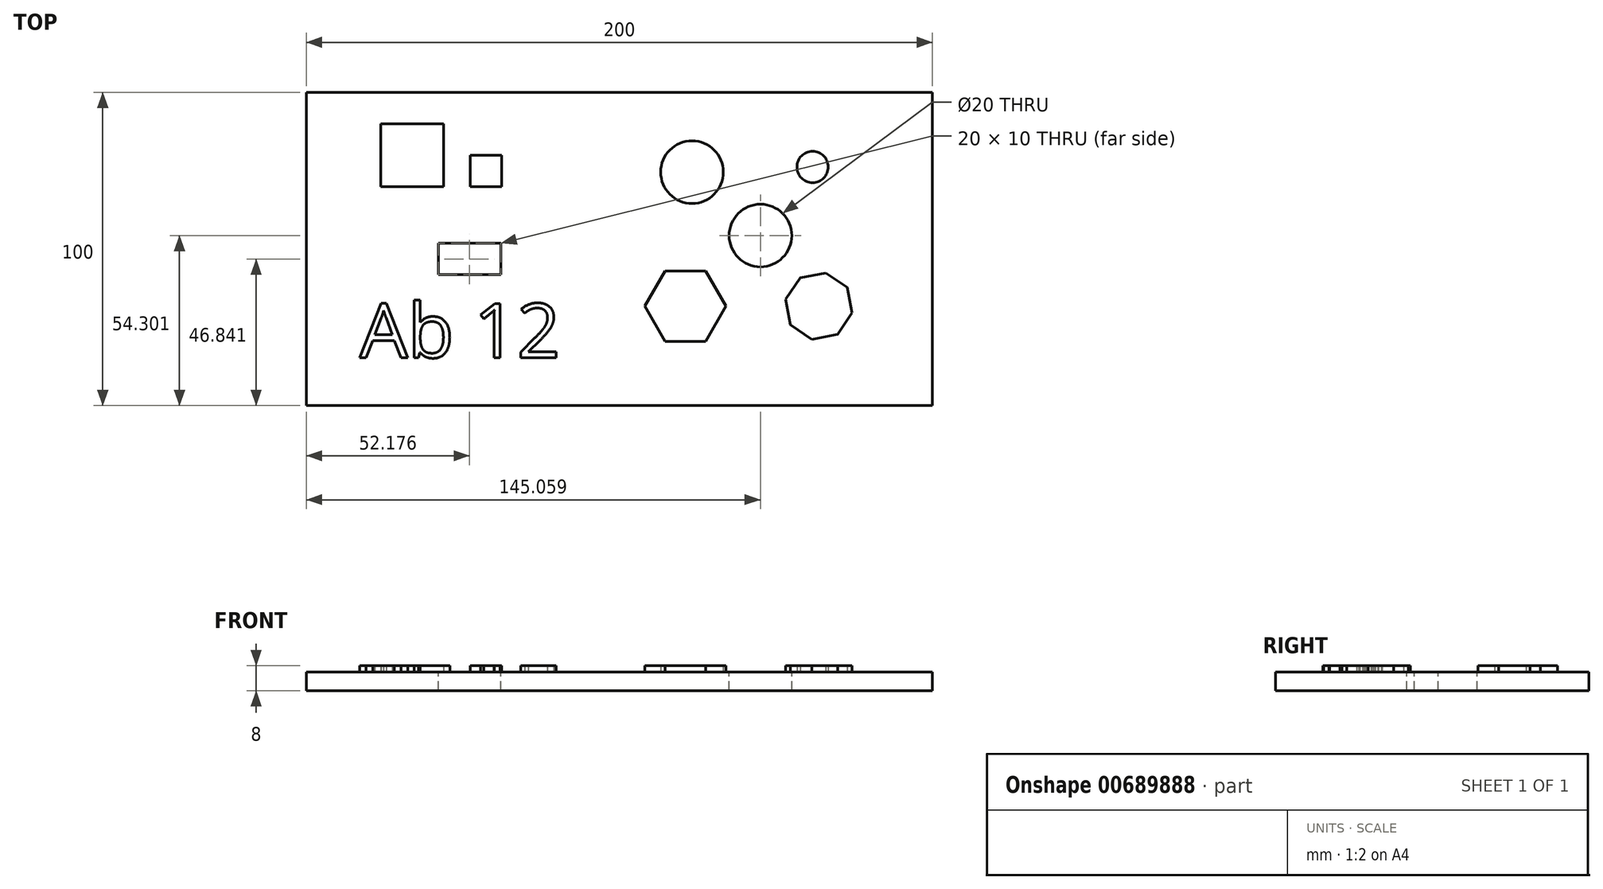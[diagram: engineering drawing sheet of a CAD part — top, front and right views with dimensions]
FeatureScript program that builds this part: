
annotation { "Feature Type Name" : "Feature", "Feature Type Description" : "" }
export const myFeature = defineFeature(function(context is Context, id is Id, definition is map)
    precondition{}
    {
        {
            var Q0;
            Q0=qCreatedBy(makeId("Top.planeOp"),FACE);
            var sketch = newSketch(context, id + "F0", { "sketchPlane" : qUnion([Q0])});
            skLineSegment(sketch, "E0.bottom", {"start": v(-100, 50) * mm, "end": v(100, 50) * mm});
            skLineSegment(sketch, "E0.top", {"start": v(-100, -50) * mm, "end": v(100, -50) * mm});
            skLineSegment(sketch, "E0.left", {"start": v(-100, 50) * mm, "end": v(-100, -50) * mm});
            skLineSegment(sketch, "E0.right", {"start": v(100, 50) * mm, "end": v(100, -50) * mm});
            skSolve(sketch);
        }
        {
            var Q0;
            Q0=makeQuery(id+"F0.imprint","IMPRINT",FACE,{"disambiguationData":[TD([[makeQuery(id+"F0.imprint","IMPRINT",EDGE,{"derivedFrom":sQuery(id+"F0.wireOp",EDGE,"E0.bottom")}),-1.0]])]});
            extrude(context, id + "F1", {"entities" : qUnion([Q0]), "depth" : 6 * mm, "offsetDistance" : 25 * mm});
        }
        {
            var Q0;
            Q0=makeQuery(id+"F1.opExtrude","CAP_FACE",FACE,{"disambiguationData":[OSD([sQuery(id+"F0.wireOp",EDGE,"E0.bottom"),sQuery(id+"F0.wireOp",EDGE,"E0.top"),sQuery(id+"F0.wireOp",EDGE,"E0.left"),sQuery(id+"F0.wireOp",EDGE,"E0.right")])],"isStart":false});
            var sketch = newSketch(context, id + "F2", { "sketchPlane" : qUnion([Q0])});
            skLineSegment(sketch, "E1.bottom", {"start": v(-76.17, 39.96) * mm, "end": v(-56.17, 39.96) * mm});
            skLineSegment(sketch, "E1.top", {"start": v(-76.17, 19.96) * mm, "end": v(-56.17, 19.96) * mm});
            skLineSegment(sketch, "E1.left", {"start": v(-76.17, 39.96) * mm, "end": v(-76.17, 19.96) * mm});
            skLineSegment(sketch, "E1.right", {"start": v(-56.17, 39.96) * mm, "end": v(-56.17, 19.96) * mm});
            skLineSegment(sketch, "E2.bottom", {"start": v(-47.63, 29.96) * mm, "end": v(-37.63, 29.96) * mm});
            skLineSegment(sketch, "E2.top", {"start": v(-47.63, 19.96) * mm, "end": v(-37.63, 19.96) * mm});
            skLineSegment(sketch, "E2.left", {"start": v(-47.63, 29.96) * mm, "end": v(-47.63, 19.96) * mm});
            skLineSegment(sketch, "E2.right", {"start": v(-37.63, 29.96) * mm, "end": v(-37.63, 19.96) * mm});
            skCircle(sketch, "E3", {"center": v(23.2, 24.54) * mm, "radius": 10 * mm});
            skCircle(sketch, "E4", {"center": v(61.7, 26.18) * mm, "radius": 5 * mm});
            skCircle(sketch, "E5.cCircle", {"center": v(21.07, -18.23) * mm, "radius": 11.24 * mm, "construction": true});
            skLineSegment(sketch, "E5.0", {"start": v(34.05, -18.21) * mm, "end": v(27.58, -29.46) * mm});
            skLineSegment(sketch, "E5.1", {"start": v(27.58, -29.46) * mm, "end": v(14.6, -29.48) * mm});
            skLineSegment(sketch, "E5.2", {"start": v(14.6, -29.48) * mm, "end": v(8.1, -18.26) * mm});
            skLineSegment(sketch, "E5.3", {"start": v(8.1, -18.26) * mm, "end": v(14.57, -7) * mm});
            skLineSegment(sketch, "E5.4", {"start": v(14.57, -7) * mm, "end": v(27.54, -6.98) * mm});
            skLineSegment(sketch, "E5.5", {"start": v(27.54, -6.98) * mm, "end": v(34.05, -18.21) * mm});
            skPoint(sketch, "E5.0.midPoint", {"position": v(30.82, -23.84) * mm});
            skCircle(sketch, "E6.cCircle", {"center": v(63.7, -18.23) * mm, "radius": 10 * mm, "construction": true});
            skLineSegment(sketch, "E6.0", {"start": v(74.3, -20.4) * mm, "end": v(69.66, -27.27) * mm});
            skLineSegment(sketch, "E6.1", {"start": v(69.66, -27.27) * mm, "end": v(61.53, -28.84) * mm});
            skLineSegment(sketch, "E6.2", {"start": v(61.53, -28.84) * mm, "end": v(54.66, -24.2) * mm});
            skLineSegment(sketch, "E6.3", {"start": v(54.66, -24.2) * mm, "end": v(53.1, -16.06) * mm});
            skLineSegment(sketch, "E6.4", {"start": v(53.1, -16.06) * mm, "end": v(57.74, -9.2) * mm});
            skLineSegment(sketch, "E6.5", {"start": v(57.74, -9.2) * mm, "end": v(65.87, -7.63) * mm});
            skLineSegment(sketch, "E6.6", {"start": v(65.87, -7.63) * mm, "end": v(72.73, -12.27) * mm});
            skLineSegment(sketch, "E6.7", {"start": v(72.73, -12.27) * mm, "end": v(74.3, -20.4) * mm});
            skPoint(sketch, "E6.0.midPoint", {"position": v(71.98, -23.84) * mm});
            skSolve(sketch);
        }
        {
            var Q0;
            Q0=makeQuery(id+"F2.imprint","IMPRINT",FACE,{"disambiguationData":[TD([[makeQuery(id+"F2.imprint","IMPRINT",EDGE,{"derivedFrom":sQuery(id+"F2.wireOp",EDGE,"E1.bottom")}),-1.0]])]});
            extrude(context, id + "F3", {"entities" : qUnion([Q0]), "operationType" : NewBodyOperationType.ADD, "depth" : 2 * mm, "offsetDistance" : 25 * mm});
        }
        {
            var Q0;
            Q0=makeQuery(id+"F2.imprint","IMPRINT",FACE,{"disambiguationData":[TD([[makeQuery(id+"F2.imprint","IMPRINT",EDGE,{"derivedFrom":sQuery(id+"F2.wireOp",EDGE,"E2.bottom")}),-1.0]])]});
            extrude(context, id + "F4", {"entities" : qUnion([Q0]), "operationType" : NewBodyOperationType.ADD, "depth" : 2 * mm, "offsetDistance" : 25 * mm});
        }
        {
            var Q0;
            Q0=makeQuery(id+"F2.imprint","IMPRINT",FACE,{"disambiguationData":[TD([[makeQuery(id+"F2.imprint","IMPRINT",EDGE,{"derivedFrom":sQuery(id+"F2.wireOp",EDGE,"E3")}),1.0]])]});
            extrude(context, id + "F5", {"entities" : qUnion([Q0]), "operationType" : NewBodyOperationType.ADD, "depth" : 2 * mm, "offsetDistance" : 25 * mm});
        }
        {
            var Q0;
            Q0=makeQuery(id+"F2.imprint","IMPRINT",FACE,{"disambiguationData":[TD([[makeQuery(id+"F2.imprint","IMPRINT",EDGE,{"derivedFrom":sQuery(id+"F2.wireOp",EDGE,"E4")}),1.0]])]});
            extrude(context, id + "F6", {"entities" : qUnion([Q0]), "operationType" : NewBodyOperationType.ADD, "depth" : 2 * mm, "offsetDistance" : 25 * mm});
        }
        {
            var Q0;
            Q0=makeQuery(id+"F2.imprint","IMPRINT",FACE,{"disambiguationData":[TD([[makeQuery(id+"F2.imprint","IMPRINT",EDGE,{"derivedFrom":sQuery(id+"F2.wireOp",EDGE,"E5.0")}),-1.0]])]});
            extrude(context, id + "F7", {"entities" : qUnion([Q0]), "operationType" : NewBodyOperationType.ADD, "depth" : 2 * mm, "offsetDistance" : 25 * mm});
        }
        {
            var Q0;
            Q0=makeQuery(id+"F2.imprint","IMPRINT",FACE,{"disambiguationData":[TD([[makeQuery(id+"F2.imprint","IMPRINT",EDGE,{"derivedFrom":sQuery(id+"F2.wireOp",EDGE,"E6.0")}),-1.0]])]});
            extrude(context, id + "F8", {"entities" : qUnion([Q0]), "operationType" : NewBodyOperationType.ADD, "depth" : 2 * mm, "offsetDistance" : 25 * mm});
        }
        {
            var Q0;
            Q0=makeQuery(id+"F2.imprint","IMPRINT",FACE,{"disambiguationData":[TD([[makeQuery(id+"F2.imprint","IMPRINT",EDGE,{"derivedFrom":sQuery(id+"F2.wireOp",EDGE,"E1.bottom")}),1.0]])]});
            var sketch = newSketch(context, id + "F9", { "sketchPlane" : qUnion([Q0])});
            skText(sketch, "E7", { "text": "Ab 12", "fontName": "OpenSans-Regular.ttf"});
            const initialGuessF9  = {"E7": [-0.08292, -0.03468, 1, 0, 0.0174]};
            skSetInitialGuess(sketch, initialGuessF9);
            skSolve(sketch);
        }
        {
            var Q0;
            Q0 = qSketchRegion(id + "F9", true);
            extrude(context, id + "F10", {"entities" : qUnion([Q0]), "operationType" : NewBodyOperationType.ADD, "depth" : 2 * mm, "offsetDistance" : 25 * mm});
        }
        {
            var Q0;
            Q0=makeQuery(id+"F2.imprint","IMPRINT",FACE,{"disambiguationData":[TD([[makeQuery(id+"F2.imprint","IMPRINT",EDGE,{"derivedFrom":sQuery(id+"F2.wireOp",EDGE,"E1.bottom")}),1.0]])]});
            var sketch = newSketch(context, id + "F11", { "sketchPlane" : qUnion([Q0])});
            skLineSegment(sketch, "E8.bottom", {"start": v(-57.82, 1.84) * mm, "end": v(-37.82, 1.84) * mm});
            skLineSegment(sketch, "E8.top", {"start": v(-57.82, -8.16) * mm, "end": v(-37.82, -8.16) * mm});
            skLineSegment(sketch, "E8.left", {"start": v(-57.82, 1.84) * mm, "end": v(-57.82, -8.16) * mm});
            skLineSegment(sketch, "E8.right", {"start": v(-37.82, 1.84) * mm, "end": v(-37.82, -8.16) * mm});
            skCircle(sketch, "E9", {"center": v(45.06, 4.3) * mm, "radius": 10 * mm});
            skSolve(sketch);
        }
        {
            var Q0;
            Q0=makeQuery(id+"F11.imprint","IMPRINT",FACE,{"disambiguationData":[TD([[makeQuery(id+"F11.imprint","IMPRINT",EDGE,{"derivedFrom":sQuery(id+"F11.wireOp",EDGE,"E8.bottom")}),-1.0]])]});
            extrude(context, id + "F12", {"entities" : qUnion([Q0]), "operationType" : NewBodyOperationType.REMOVE, "oppositeDirection" : true, "depth" : 25 * mm, "offsetDistance" : 25 * mm});
        }
        {
            var Q0;
            Q0=makeQuery(id+"F11.imprint","IMPRINT",FACE,{"disambiguationData":[TD([[makeQuery(id+"F11.imprint","IMPRINT",EDGE,{"derivedFrom":sQuery(id+"F11.wireOp",EDGE,"E9")}),1.0]])]});
            extrude(context, id + "F13", {"entities" : qUnion([Q0]), "operationType" : NewBodyOperationType.REMOVE, "oppositeDirection" : true, "depth" : 25 * mm, "offsetDistance" : 25 * mm, "hasSecondDirection" : true, "secondDirectionOppositeDirection" : false, "secondDirectionDepth" : 25 * mm});
        }
    });
